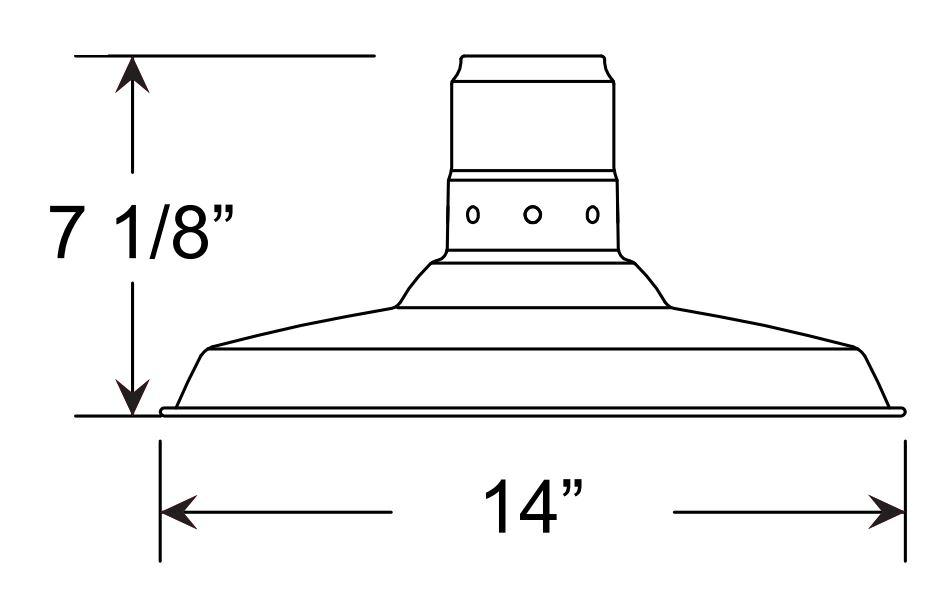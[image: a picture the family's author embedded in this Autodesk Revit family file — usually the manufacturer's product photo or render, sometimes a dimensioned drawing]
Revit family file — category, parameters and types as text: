
# Revit family: Orbitor T 200w -218,220 MB
name_source: partatom
category: Lighting Fixtures
units: mm (PartAtom-declared; Revit-internal decimal feet)

## family parameters
Always vertical = Yes
Cut with Voids When Loaded = No
Light Source = Yes
OmniClass Number = 23.80.70.00
OmniClass Title = Lighting
Part Type = Normal
Room Calculation Point = No
Round Connector Dimension = Use Diameter
Shared = No
Work Plane-Based = No

## types (2) — shared parameters
Apparent Load = 200 VA
Body Colour = Spun aluminium
Body Material = body
Bulb = Bulb
CRI = >90
Color Filter = 16777215
Construction Material = Heavy Duty spun aluminum.
Default Elevation = 0' - 0"
Description = 120-277 Voltage
Dimming = 1%
Dimming Lamp Color Temperature Shift = <None>
Efficiency = 65-125 lumens per watt
INSIDE BODY = INSIDE BODY
Lamp = MB
Life = L70 50,000 hours
Load Classification = Lighting
Manufacturer = ANP Lighting
Photometric Web File = generic.ies
Power Factor = 1
Tilt Angle = 90.00°
URL = https://www.anplighting.com
Voltage = 277 V
Warranty = 5 year limited warranty
Wattage Comments = 200W Max
Weight = 3.0 lbs

## per-type parameters (varying)
| type | Fixture Diameter | Fixture Height | Model | ORBITOR18 | ORBITOR20 |
| ORB218 | 1' - 6" | 1' - 2" | ORBT218 | Yes | No |
| ORB220 | 1' - 8" | 1' - 2 1/2" | ORBT220 | No | Yes |

## geometry (parser evidence)
native form markers: Sweep x28
no freeform markers — native parametric forms only
